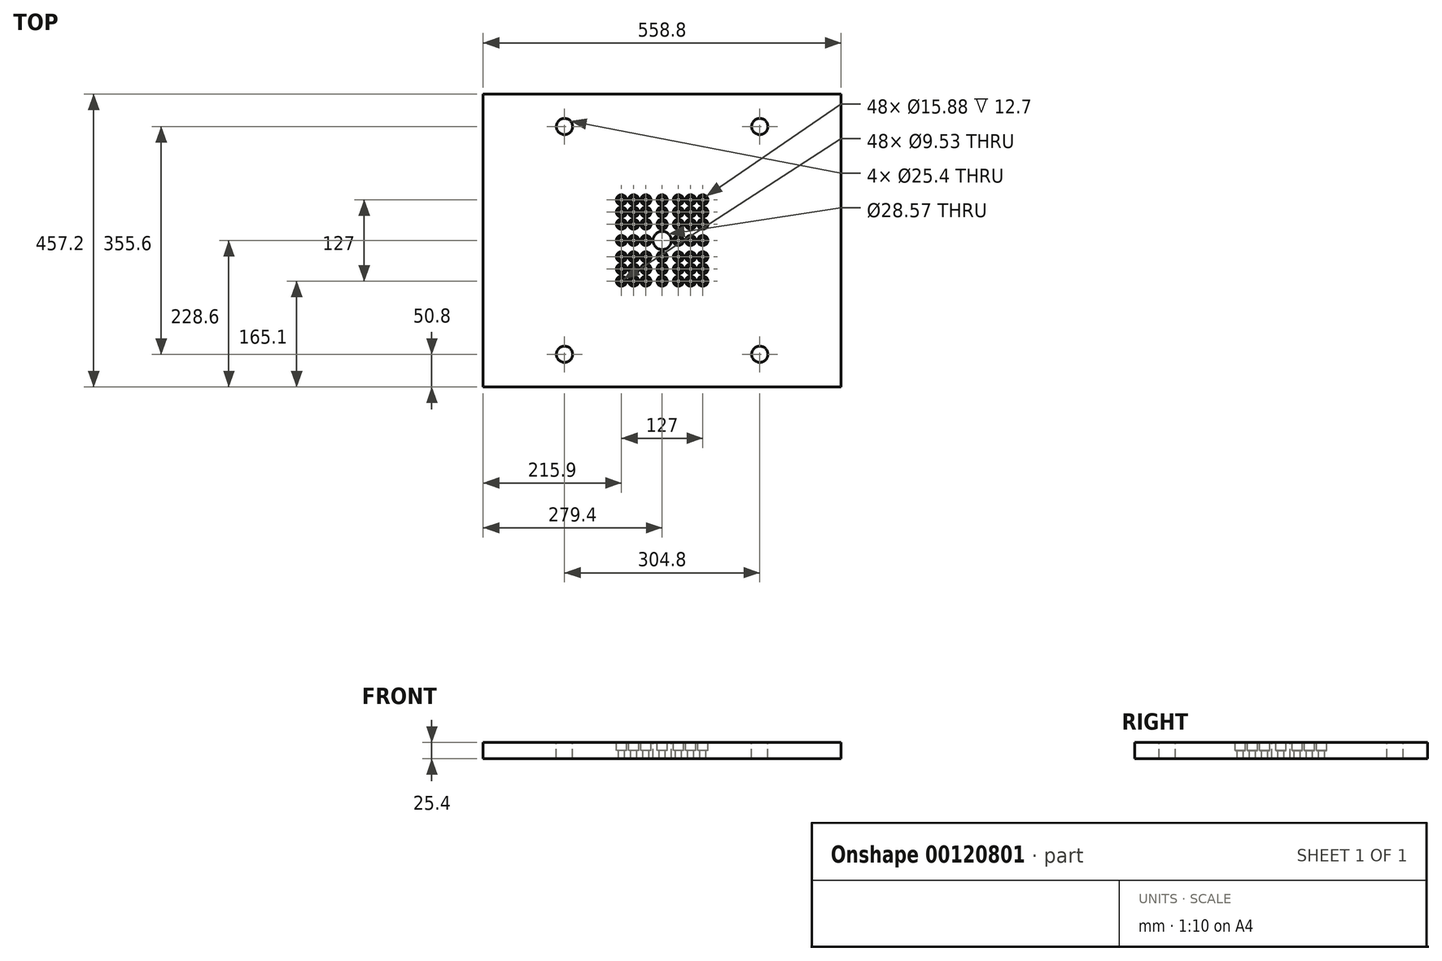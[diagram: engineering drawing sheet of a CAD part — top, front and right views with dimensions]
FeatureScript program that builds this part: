
annotation { "Feature Type Name" : "Feature", "Feature Type Description" : "" }
export const myFeature = defineFeature(function(context is Context, id is Id, definition is map)
    precondition{}
    {
        {
            var Q0;
            Q0=qCreatedBy(makeId("Top.planeOp"),FACE);
            var sketch = newSketch(context, id + "F0", { "sketchPlane" : qUnion([Q0])});
            skLineSegment(sketch, "E0.bottom", {"start": v(279.4, -228.6) * mm, "end": v(-279.4, -228.6) * mm});
            skLineSegment(sketch, "E0.top", {"start": v(279.4, 228.6) * mm, "end": v(-279.4, 228.6) * mm});
            skLineSegment(sketch, "E0.left", {"start": v(279.4, -228.6) * mm, "end": v(279.4, 228.6) * mm});
            skLineSegment(sketch, "E0.right", {"start": v(-279.4, -228.6) * mm, "end": v(-279.4, 228.6) * mm});
            skPoint(sketch, "E0.middle", {"position": v(0, 0) * mm});
            skSolve(sketch);
        }
        {
            var Q0;
            Q0 = qSketchRegion(id + "F0", true);
            extrude(context, id + "F1", {"entities" : qUnion([Q0]), "oppositeDirection" : true, "depth" : 25.4 * mm});
        }
        {
            var Q0;
            Q0=makeQuery(id+"F1.opExtrude","CAP_FACE",FACE,{"disambiguationData":[OSD([sQuery(id+"F0.wireOp",EDGE,"E0.bottom"),sQuery(id+"F0.wireOp",EDGE,"E0.top"),sQuery(id+"F0.wireOp",EDGE,"E0.left"),sQuery(id+"F0.wireOp",EDGE,"E0.right")])],"isStart":true});
            var sketch = newSketch(context, id + "F2", { "sketchPlane" : qUnion([Q0])});
            skCircle(sketch, "E1", {"center": v(-152.4, -177.8) * mm, "radius": 12.7 * mm});
            skCircle(sketch, "E2", {"center": v(152.4, -177.8) * mm, "radius": 12.7 * mm});
            skCircle(sketch, "E3", {"center": v(-152.4, 177.8) * mm, "radius": 12.7 * mm});
            skCircle(sketch, "E4", {"center": v(152.4, 177.8) * mm, "radius": 12.7 * mm});
            skLineSegment(sketch, "E5", {"start": v(-152.4, -177.8) * mm, "end": v(-279.4, -177.8) * mm});
            skLineSegment(sketch, "E6", {"start": v(152.4, -177.8) * mm, "end": v(279.4, -177.8) * mm});
            skSolve(sketch);
        }
        {
            var Q0;
            Q0 = qSketchRegion(id + "F2", true);
            extrude(context, id + "F3", {"entities" : qUnion([Q0]), "operationType" : NewBodyOperationType.REMOVE, "endBound" : BoundingType.THROUGH_ALL, "oppositeDirection" : true, "depth" : 25.4 * mm});
        }
        {
            var Q0;
            Q0=makeQuery(id+"F1.opExtrude","CAP_FACE",FACE,{"disambiguationData":[OSD([sQuery(id+"F0.wireOp",EDGE,"E0.bottom"),sQuery(id+"F0.wireOp",EDGE,"E0.top"),sQuery(id+"F0.wireOp",EDGE,"E0.left"),sQuery(id+"F0.wireOp",EDGE,"E0.right")])],"isStart":true});
            var sketch = newSketch(context, id + "F4", { "sketchPlane" : qUnion([Q0])});
            skCircle(sketch, "E7", {"center": v(25.4, 63.5) * mm, "radius": 7.94 * mm});
            skCircle(sketch, "E8", {"center": v(25.4, 44.45) * mm, "radius": 7.94 * mm});
            skCircle(sketch, "E9", {"center": v(25.4, 25.4) * mm, "radius": 7.94 * mm});
            skCircle(sketch, "E10", {"center": v(44.45, 63.5) * mm, "radius": 7.94 * mm});
            skCircle(sketch, "E11", {"center": v(63.5, 63.5) * mm, "radius": 7.94 * mm});
            skCircle(sketch, "E12", {"center": v(44.45, 44.45) * mm, "radius": 7.94 * mm});
            skCircle(sketch, "E13", {"center": v(63.5, 44.45) * mm, "radius": 7.94 * mm});
            skCircle(sketch, "E14", {"center": v(44.45, 25.4) * mm, "radius": 7.94 * mm});
            skCircle(sketch, "E15", {"center": v(63.5, 25.4) * mm, "radius": 7.94 * mm});
            skCircle(sketch, "E16", {"center": v(0, 0) * mm, "radius": 14.29 * mm});
            skCircle(sketch, "E17", {"center": v(25.4, 0) * mm, "radius": 7.94 * mm});
            skCircle(sketch, "E18", {"center": v(44.45, 0) * mm, "radius": 7.94 * mm});
            skCircle(sketch, "E19", {"center": v(63.5, 0) * mm, "radius": 7.94 * mm});
            skCircle(sketch, "E20", {"center": v(0, 25.4) * mm, "radius": 7.94 * mm});
            skCircle(sketch, "E21", {"center": v(0, 44.45) * mm, "radius": 7.94 * mm});
            skCircle(sketch, "E22", {"center": v(0, 63.5) * mm, "radius": 7.94 * mm});
            skLineSegment(sketch, "E23", {"start": v(0, 63.5) * mm, "end": v(0, 25.4) * mm});
            skLineSegment(sketch, "E24", {"start": v(25.4, 0) * mm, "end": v(63.5, 0) * mm});
            skCircle(sketch, "E25.MirrorC", {"center": v(-25.4, 44.45) * mm, "radius": 7.94 * mm});
            skCircle(sketch, "E26.MirrorC", {"center": v(-25.4, 63.5) * mm, "radius": 7.94 * mm});
            skCircle(sketch, "E27.MirrorC", {"center": v(-44.45, 63.5) * mm, "radius": 7.94 * mm});
            skCircle(sketch, "E28.MirrorC", {"center": v(-63.5, 63.5) * mm, "radius": 7.94 * mm});
            skCircle(sketch, "E29.MirrorC", {"center": v(-63.5, 44.45) * mm, "radius": 7.94 * mm});
            skCircle(sketch, "E30.MirrorC", {"center": v(-63.5, 25.4) * mm, "radius": 7.94 * mm});
            skCircle(sketch, "E31.MirrorC", {"center": v(-44.45, 25.4) * mm, "radius": 7.94 * mm});
            skCircle(sketch, "E32.MirrorC", {"center": v(-25.4, 25.4) * mm, "radius": 7.94 * mm});
            skCircle(sketch, "E33.MirrorC", {"center": v(-44.45, 44.45) * mm, "radius": 7.94 * mm});
            skLineSegment(sketch, "E34.MirrorCS", {"start": v(0, -63.5) * mm, "end": v(0, -25.4) * mm});
            skCircle(sketch, "E35.MirrorC", {"center": v(-25.4, -25.4) * mm, "radius": 7.94 * mm});
            skCircle(sketch, "E36.MirrorC", {"center": v(-63.5, -44.45) * mm, "radius": 7.94 * mm});
            skCircle(sketch, "E37.MirrorC", {"center": v(-44.45, -63.5) * mm, "radius": 7.94 * mm});
            skCircle(sketch, "E38.MirrorC", {"center": v(-25.4, -63.5) * mm, "radius": 7.94 * mm});
            skCircle(sketch, "E39.MirrorC", {"center": v(-25.4, -44.45) * mm, "radius": 7.94 * mm});
            skCircle(sketch, "E40.MirrorC", {"center": v(-63.5, -63.5) * mm, "radius": 7.94 * mm});
            skCircle(sketch, "E41.MirrorC", {"center": v(-44.45, -25.4) * mm, "radius": 7.94 * mm});
            skCircle(sketch, "E42.MirrorC", {"center": v(0, -25.4) * mm, "radius": 7.94 * mm});
            skCircle(sketch, "E43.MirrorC", {"center": v(0, -44.45) * mm, "radius": 7.94 * mm});
            skCircle(sketch, "E44.MirrorC", {"center": v(0, -63.5) * mm, "radius": 7.94 * mm});
            skCircle(sketch, "E45.MirrorC", {"center": v(25.4, -63.5) * mm, "radius": 7.94 * mm});
            skCircle(sketch, "E46.MirrorC", {"center": v(25.4, -44.45) * mm, "radius": 7.94 * mm});
            skCircle(sketch, "E47.MirrorC", {"center": v(-63.5, -25.4) * mm, "radius": 7.94 * mm});
            skCircle(sketch, "E48.MirrorC", {"center": v(25.4, -25.4) * mm, "radius": 7.94 * mm});
            skCircle(sketch, "E49.MirrorC", {"center": v(44.45, -63.5) * mm, "radius": 7.94 * mm});
            skCircle(sketch, "E50.MirrorC", {"center": v(63.5, -63.5) * mm, "radius": 7.94 * mm});
            skCircle(sketch, "E51.MirrorC", {"center": v(44.45, -44.45) * mm, "radius": 7.94 * mm});
            skCircle(sketch, "E52.MirrorC", {"center": v(63.5, -44.45) * mm, "radius": 7.94 * mm});
            skCircle(sketch, "E53.MirrorC", {"center": v(-44.45, -44.45) * mm, "radius": 7.94 * mm});
            skCircle(sketch, "E54.MirrorC", {"center": v(44.45, -25.4) * mm, "radius": 7.94 * mm});
            skCircle(sketch, "E55.MirrorC", {"center": v(63.5, -25.4) * mm, "radius": 7.94 * mm});
            skCircle(sketch, "E56.MirrorC", {"center": v(-25.4, 0) * mm, "radius": 7.94 * mm});
            skCircle(sketch, "E57.MirrorC", {"center": v(-44.45, 0) * mm, "radius": 7.94 * mm});
            skCircle(sketch, "E58.MirrorC", {"center": v(-63.5, 0) * mm, "radius": 7.94 * mm});
            skSolve(sketch);
        }
        {
            var Q0;
            Q0 = qSketchRegion(id + "F4", true);
            extrude(context, id + "F5", {"entities" : qUnion([Q0]), "operationType" : NewBodyOperationType.REMOVE, "endBound" : BoundingType.THROUGH_ALL, "oppositeDirection" : true, "depth" : 25.4 * mm});
        }
        {
            var Q0;
            Q0=makeQuery(id+"F1.opExtrude","CAP_FACE",FACE,{"disambiguationData":[OSD([sQuery(id+"F0.wireOp",EDGE,"E0.bottom"),sQuery(id+"F0.wireOp",EDGE,"E0.top"),sQuery(id+"F0.wireOp",EDGE,"E0.left"),sQuery(id+"F0.wireOp",EDGE,"E0.right")])],"isStart":true});
            cPlane(context, id + "F6", {"entities" : qUnion([Q0]), "cplaneType" : CPlaneType.OFFSET, "offset" : 12.7 * mm, "oppositeDirection" : true, "width" : 152.4 * mm, "height" : 152.4 * mm});
        }
        {
            var Q0;
            Q0=qCreatedBy(id+"F6.planeOp",FACE);
            var sketch = newSketch(context, id + "F7", { "sketchPlane" : qUnion([Q0])});
            skCircle(sketch, "E59.0", {"center": v(63.5, 63.5) * mm, "radius": 7.94 * mm});
            skCircle(sketch, "E59.1", {"center": v(63.5, 44.45) * mm, "radius": 7.94 * mm});
            skCircle(sketch, "E59.2", {"center": v(44.45, 44.45) * mm, "radius": 7.94 * mm});
            skCircle(sketch, "E59.3", {"center": v(44.45, 25.4) * mm, "radius": 7.94 * mm});
            skCircle(sketch, "E59.4", {"center": v(44.45, 63.5) * mm, "radius": 7.94 * mm});
            skCircle(sketch, "E59.5", {"center": v(25.4, 63.5) * mm, "radius": 7.94 * mm});
            skCircle(sketch, "E59.6", {"center": v(25.4, 44.45) * mm, "radius": 7.94 * mm});
            skCircle(sketch, "E59.7", {"center": v(25.4, 25.4) * mm, "radius": 7.94 * mm});
            skCircle(sketch, "E59.8", {"center": v(63.5, 25.4) * mm, "radius": 7.94 * mm});
            skCircle(sketch, "E59.9", {"center": v(63.5, 0) * mm, "radius": 7.94 * mm});
            skCircle(sketch, "E59.10", {"center": v(44.45, 0) * mm, "radius": 7.94 * mm});
            skCircle(sketch, "E59.11", {"center": v(25.4, 0) * mm, "radius": 7.94 * mm});
            skCircle(sketch, "E59.12", {"center": v(25.4, -25.4) * mm, "radius": 7.94 * mm});
            skCircle(sketch, "E59.13", {"center": v(44.45, -25.4) * mm, "radius": 7.94 * mm});
            skCircle(sketch, "E59.14", {"center": v(63.5, -25.4) * mm, "radius": 7.94 * mm});
            skCircle(sketch, "E59.15", {"center": v(63.5, -44.45) * mm, "radius": 7.94 * mm});
            skCircle(sketch, "E59.16", {"center": v(44.45, -44.45) * mm, "radius": 7.94 * mm});
            skCircle(sketch, "E59.17", {"center": v(25.4, -44.45) * mm, "radius": 7.94 * mm});
            skCircle(sketch, "E59.18", {"center": v(25.4, -63.5) * mm, "radius": 7.94 * mm});
            skCircle(sketch, "E59.19", {"center": v(44.45, -63.5) * mm, "radius": 7.94 * mm});
            skCircle(sketch, "E59.20", {"center": v(63.5, -63.5) * mm, "radius": 7.94 * mm});
            skCircle(sketch, "E59.21", {"center": v(0, -63.5) * mm, "radius": 7.94 * mm});
            skCircle(sketch, "E59.22", {"center": v(0, -44.45) * mm, "radius": 7.94 * mm});
            skCircle(sketch, "E59.23", {"center": v(0, -25.4) * mm, "radius": 7.94 * mm});
            skCircle(sketch, "E59.24", {"center": v(0, 25.4) * mm, "radius": 7.94 * mm});
            skCircle(sketch, "E59.25", {"center": v(0, 44.45) * mm, "radius": 7.94 * mm});
            skCircle(sketch, "E59.26", {"center": v(0, 63.5) * mm, "radius": 7.94 * mm});
            skCircle(sketch, "E59.27", {"center": v(-25.4, 63.5) * mm, "radius": 7.94 * mm});
            skCircle(sketch, "E59.28", {"center": v(-25.4, 44.45) * mm, "radius": 7.94 * mm});
            skCircle(sketch, "E59.29", {"center": v(-25.4, 25.4) * mm, "radius": 7.94 * mm});
            skCircle(sketch, "E59.30", {"center": v(-25.4, 0) * mm, "radius": 7.94 * mm});
            skCircle(sketch, "E59.31", {"center": v(-25.4, -25.4) * mm, "radius": 7.94 * mm});
            skCircle(sketch, "E59.32", {"center": v(-25.4, -44.45) * mm, "radius": 7.94 * mm});
            skCircle(sketch, "E59.33", {"center": v(-25.4, -63.5) * mm, "radius": 7.94 * mm});
            skCircle(sketch, "E59.34", {"center": v(-44.45, -63.5) * mm, "radius": 7.94 * mm});
            skCircle(sketch, "E59.35", {"center": v(-44.45, -44.45) * mm, "radius": 7.94 * mm});
            skCircle(sketch, "E59.36", {"center": v(-44.45, -25.4) * mm, "radius": 7.94 * mm});
            skCircle(sketch, "E59.37", {"center": v(-44.45, 0) * mm, "radius": 7.94 * mm});
            skCircle(sketch, "E59.38", {"center": v(-44.45, 25.4) * mm, "radius": 7.94 * mm});
            skCircle(sketch, "E59.39", {"center": v(-44.45, 44.45) * mm, "radius": 7.94 * mm});
            skCircle(sketch, "E59.40", {"center": v(-44.45, 63.5) * mm, "radius": 7.94 * mm});
            skCircle(sketch, "E59.41", {"center": v(-63.5, 63.5) * mm, "radius": 7.94 * mm});
            skCircle(sketch, "E59.42", {"center": v(-63.5, 44.45) * mm, "radius": 7.94 * mm});
            skCircle(sketch, "E59.43", {"center": v(-63.5, 25.4) * mm, "radius": 7.94 * mm});
            skCircle(sketch, "E59.44", {"center": v(-63.5, 0) * mm, "radius": 7.94 * mm});
            skCircle(sketch, "E59.45", {"center": v(-63.5, -25.4) * mm, "radius": 7.94 * mm});
            skCircle(sketch, "E59.46", {"center": v(-63.5, -44.45) * mm, "radius": 7.94 * mm});
            skCircle(sketch, "E59.47", {"center": v(-63.5, -63.5) * mm, "radius": 7.94 * mm});
            skCircle(sketch, "E60", {"center": v(63.5, 63.5) * mm, "radius": 4.76 * mm});
            skCircle(sketch, "E61", {"center": v(63.5, 44.45) * mm, "radius": 4.76 * mm});
            skCircle(sketch, "E62", {"center": v(63.5, 25.4) * mm, "radius": 4.76 * mm});
            skCircle(sketch, "E63", {"center": v(44.45, 25.4) * mm, "radius": 4.76 * mm});
            skCircle(sketch, "E64", {"center": v(44.45, 63.5) * mm, "radius": 4.76 * mm});
            skCircle(sketch, "E65", {"center": v(44.45, 44.45) * mm, "radius": 4.76 * mm});
            skCircle(sketch, "E66", {"center": v(25.4, 63.5) * mm, "radius": 4.76 * mm});
            skCircle(sketch, "E67", {"center": v(25.4, 44.45) * mm, "radius": 4.76 * mm});
            skCircle(sketch, "E68", {"center": v(25.4, 25.4) * mm, "radius": 4.76 * mm});
            skCircle(sketch, "E69", {"center": v(0, 63.5) * mm, "radius": 4.76 * mm});
            skCircle(sketch, "E70", {"center": v(0, 44.45) * mm, "radius": 4.76 * mm});
            skCircle(sketch, "E71", {"center": v(0, 25.4) * mm, "radius": 4.76 * mm});
            skCircle(sketch, "E72", {"center": v(63.5, 0) * mm, "radius": 4.76 * mm});
            skCircle(sketch, "E73", {"center": v(44.45, 0) * mm, "radius": 4.76 * mm});
            skCircle(sketch, "E74", {"center": v(25.4, 0) * mm, "radius": 4.76 * mm});
            skLineSegment(sketch, "E75", {"start": v(0, 63.5) * mm, "end": v(0, 25.4) * mm});
            skLineSegment(sketch, "E76", {"start": v(25.4, 0) * mm, "end": v(63.5, 0) * mm});
            skCircle(sketch, "E77.MirrorC", {"center": v(-25.4, 63.5) * mm, "radius": 4.76 * mm});
            skCircle(sketch, "E78.MirrorC", {"center": v(-44.45, 63.5) * mm, "radius": 4.76 * mm});
            skCircle(sketch, "E79.MirrorC", {"center": v(-63.5, 63.5) * mm, "radius": 4.76 * mm});
            skCircle(sketch, "E80.MirrorC", {"center": v(-63.5, 44.45) * mm, "radius": 4.76 * mm});
            skCircle(sketch, "E81.MirrorC", {"center": v(-44.45, 44.45) * mm, "radius": 4.76 * mm});
            skCircle(sketch, "E82.MirrorC", {"center": v(-25.4, 44.45) * mm, "radius": 4.76 * mm});
            skCircle(sketch, "E83.MirrorC", {"center": v(-25.4, 25.4) * mm, "radius": 4.76 * mm});
            skCircle(sketch, "E84.MirrorC", {"center": v(-44.45, 25.4) * mm, "radius": 4.76 * mm});
            skCircle(sketch, "E85.MirrorC", {"center": v(-63.5, 25.4) * mm, "radius": 4.76 * mm});
            skCircle(sketch, "E86.MirrorC", {"center": v(63.5, -25.4) * mm, "radius": 4.76 * mm});
            skCircle(sketch, "E87.MirrorC", {"center": v(63.5, -44.45) * mm, "radius": 4.76 * mm});
            skCircle(sketch, "E88.MirrorC", {"center": v(63.5, -63.5) * mm, "radius": 4.76 * mm});
            skCircle(sketch, "E89.MirrorC", {"center": v(44.45, -63.5) * mm, "radius": 4.76 * mm});
            skCircle(sketch, "E90.MirrorC", {"center": v(44.45, -44.45) * mm, "radius": 4.76 * mm});
            skCircle(sketch, "E91.MirrorC", {"center": v(44.45, -25.4) * mm, "radius": 4.76 * mm});
            skCircle(sketch, "E92.MirrorC", {"center": v(25.4, -25.4) * mm, "radius": 4.76 * mm});
            skCircle(sketch, "E93.MirrorC", {"center": v(25.4, -44.45) * mm, "radius": 4.76 * mm});
            skCircle(sketch, "E94.MirrorC", {"center": v(25.4, -63.5) * mm, "radius": 4.76 * mm});
            skCircle(sketch, "E95.MirrorC", {"center": v(0, -63.5) * mm, "radius": 4.76 * mm});
            skCircle(sketch, "E96.MirrorC", {"center": v(0, -44.45) * mm, "radius": 4.76 * mm});
            skCircle(sketch, "E97.MirrorC", {"center": v(0, -25.4) * mm, "radius": 4.76 * mm});
            skCircle(sketch, "E98.MirrorC", {"center": v(-25.4, -25.4) * mm, "radius": 4.76 * mm});
            skCircle(sketch, "E99.MirrorC", {"center": v(-25.4, -44.45) * mm, "radius": 4.76 * mm});
            skCircle(sketch, "E100.MirrorC", {"center": v(-25.4, -63.5) * mm, "radius": 4.76 * mm});
            skCircle(sketch, "E101.MirrorC", {"center": v(-44.45, -63.5) * mm, "radius": 4.76 * mm});
            skCircle(sketch, "E102.MirrorC", {"center": v(-44.45, -44.45) * mm, "radius": 4.76 * mm});
            skCircle(sketch, "E103.MirrorC", {"center": v(-44.45, -25.4) * mm, "radius": 4.76 * mm});
            skCircle(sketch, "E104.MirrorC", {"center": v(-63.5, -25.4) * mm, "radius": 4.76 * mm});
            skCircle(sketch, "E105.MirrorC", {"center": v(-63.5, -44.45) * mm, "radius": 4.76 * mm});
            skCircle(sketch, "E106.MirrorC", {"center": v(-63.5, -63.5) * mm, "radius": 4.76 * mm});
            skCircle(sketch, "E107.MirrorC", {"center": v(-25.4, 0) * mm, "radius": 4.76 * mm});
            skCircle(sketch, "E108.MirrorC", {"center": v(-44.45, 0) * mm, "radius": 4.76 * mm});
            skCircle(sketch, "E109.MirrorC", {"center": v(-63.5, 0) * mm, "radius": 4.76 * mm});
            skSolve(sketch);
        }
        {
            var Q0;
            Q0 = qSketchRegion(id + "F7", true);
            extrude(context, id + "F8", {"entities" : qUnion([Q0]), "operationType" : NewBodyOperationType.ADD, "oppositeDirection" : true, "depth" : 12.7 * mm});
        }
    });
